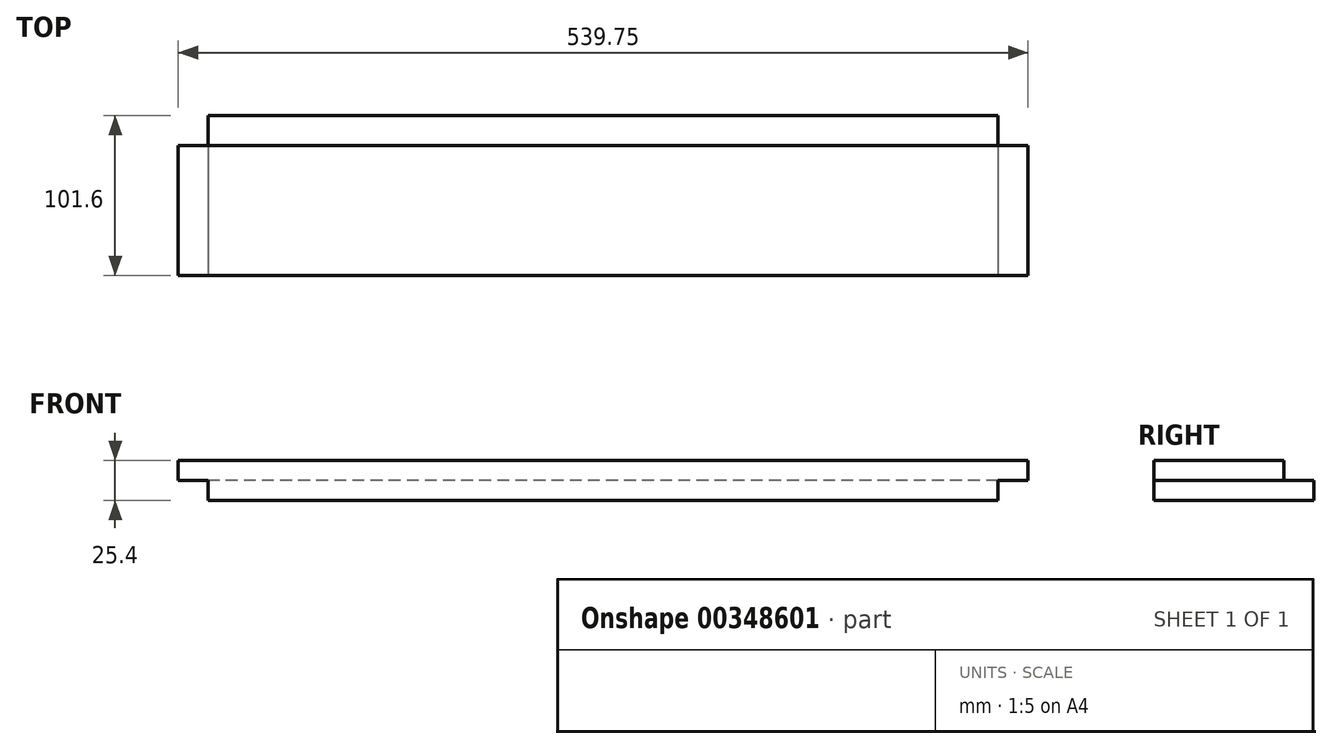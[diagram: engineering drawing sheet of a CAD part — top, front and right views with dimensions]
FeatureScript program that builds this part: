
annotation { "Feature Type Name" : "Feature", "Feature Type Description" : "" }
export const myFeature = defineFeature(function(context is Context, id is Id, definition is map)
    precondition{}
    {
        {
            var Q0;
            Q0=qCreatedBy(makeId("Top.planeOp"),FACE);
            var sketch = newSketch(context, id + "F0", { "sketchPlane" : qUnion([Q0])});
            skLineSegment(sketch, "E0.bottom", {"start": v(-320.57, -5.97) * mm, "end": v(219.18, -5.97) * mm});
            skLineSegment(sketch, "E0.top", {"start": v(-320.57, -107.57) * mm, "end": v(219.18, -107.57) * mm});
            skLineSegment(sketch, "E0.left", {"start": v(-320.57, -5.97) * mm, "end": v(-320.57, -107.57) * mm});
            skLineSegment(sketch, "E0.right", {"start": v(219.18, -5.97) * mm, "end": v(219.18, -107.57) * mm});
            skLineSegment(sketch, "E1", {"start": v(-301.52, -5.97) * mm, "end": v(-301.52, -107.57) * mm});
            skLineSegment(sketch, "E2", {"start": v(200.13, -5.97) * mm, "end": v(200.13, -107.57) * mm});
            skLineSegment(sketch, "E3", {"start": v(-320.57, -25.02) * mm, "end": v(219.18, -25.02) * mm});
            skSolve(sketch);
        }
        {
            var Q0;
            {var subQ0=sQuery(id+"F0.wireOp",EDGE,"E1");var subQ1=sQuery(id+"F0.wireOp",EDGE,"E0.top");var subQ2=makeQuery(id+"F0.imprint","INTERSECT",VERTEX,{"derivedFrom":[subQ1,subQ0]});Q0=makeQuery(id+"F0.imprint","IMPRINT",FACE,{"disambiguationData":[TD([[makeQuery(id+"F0.imprint","IMPRINT",EDGE,{"disambiguationData":[TD([[subQ2,-1.0]])],"derivedFrom":subQ1}),1.0]])]});}
            var Q1;
            {var subQ0=sQuery(id+"F0.wireOp",EDGE,"E0.left");var subQ1=sQuery(id+"F0.wireOp",EDGE,"E0.top");var subQ2=makeQuery(id+"F0.imprint","INTERSECT",VERTEX,{"derivedFrom":[subQ1,subQ0]});Q1=makeQuery(id+"F0.imprint","IMPRINT",FACE,{"disambiguationData":[TD([[makeQuery(id+"F0.imprint","IMPRINT",EDGE,{"disambiguationData":[TD([[subQ2,-1.0]])],"derivedFrom":subQ1}),1.0]])]});}
            var Q2;
            {var subQ0=sQuery(id+"F0.wireOp",EDGE,"E1");var subQ1=sQuery(id+"F0.wireOp",EDGE,"E0.bottom");var subQ2=makeQuery(id+"F0.imprint","INTERSECT",VERTEX,{"derivedFrom":[subQ1,subQ0]});Q2=makeQuery(id+"F0.imprint","IMPRINT",FACE,{"disambiguationData":[TD([[makeQuery(id+"F0.imprint","IMPRINT",EDGE,{"disambiguationData":[TD([[subQ2,-1.0]])],"derivedFrom":subQ1}),-1.0]])]});}
            var Q3;
            {var subQ0=sQuery(id+"F0.wireOp",EDGE,"E0.right");var subQ1=sQuery(id+"F0.wireOp",EDGE,"E0.top");var subQ2=makeQuery(id+"F0.imprint","INTERSECT",VERTEX,{"derivedFrom":[subQ1,subQ0]});Q3=makeQuery(id+"F0.imprint","IMPRINT",FACE,{"disambiguationData":[TD([[makeQuery(id+"F0.imprint","IMPRINT",EDGE,{"disambiguationData":[TD([[subQ2,1.0]])],"derivedFrom":subQ1}),1.0]])]});}
            extrude(context, id + "F1", {"entities" : qUnion([Q0, Q1, Q2, Q3]), "depth" : 12.7 * mm});
        }
        {
            var Q0;
            {var subQ0=sQuery(id+"F0.wireOp",EDGE,"E1");var subQ1=sQuery(id+"F0.wireOp",EDGE,"E0.top");var subQ2=makeQuery(id+"F0.imprint","INTERSECT",VERTEX,{"derivedFrom":[subQ1,subQ0]});Q0=makeQuery(id+"F0.imprint","IMPRINT",FACE,{"disambiguationData":[TD([[makeQuery(id+"F0.imprint","IMPRINT",EDGE,{"disambiguationData":[TD([[subQ2,-1.0]])],"derivedFrom":subQ1}),1.0]])]});}
            var Q1;
            {var subQ0=sQuery(id+"F0.wireOp",EDGE,"E0.left");var subQ1=sQuery(id+"F0.wireOp",EDGE,"E0.top");var subQ2=makeQuery(id+"F0.imprint","INTERSECT",VERTEX,{"derivedFrom":[subQ1,subQ0]});Q1=makeQuery(id+"F0.imprint","IMPRINT",FACE,{"disambiguationData":[TD([[makeQuery(id+"F0.imprint","IMPRINT",EDGE,{"disambiguationData":[TD([[subQ2,-1.0]])],"derivedFrom":subQ1}),1.0]])]});}
            var Q2;
            {var subQ0=sQuery(id+"F0.wireOp",EDGE,"E0.right");var subQ1=sQuery(id+"F0.wireOp",EDGE,"E0.top");var subQ2=makeQuery(id+"F0.imprint","INTERSECT",VERTEX,{"derivedFrom":[subQ1,subQ0]});Q2=makeQuery(id+"F0.imprint","IMPRINT",FACE,{"disambiguationData":[TD([[makeQuery(id+"F0.imprint","IMPRINT",EDGE,{"disambiguationData":[TD([[subQ2,1.0]])],"derivedFrom":subQ1}),1.0]])]});}
            extrude(context, id + "F2", {"entities" : qUnion([Q0, Q1, Q2]), "operationType" : NewBodyOperationType.ADD, "depth" : 25.4 * mm});
        }
        {
            var Q0;
            {var subQ0=sQuery(id+"F0.wireOp",EDGE,"E0.left");var subQ1=sQuery(id+"F0.wireOp",EDGE,"E0.top");var subQ2=makeQuery(id+"F0.imprint","INTERSECT",VERTEX,{"derivedFrom":[subQ1,subQ0]});Q0=makeQuery(id+"F0.imprint","IMPRINT",FACE,{"disambiguationData":[TD([[makeQuery(id+"F0.imprint","IMPRINT",EDGE,{"disambiguationData":[TD([[subQ2,-1.0]])],"derivedFrom":subQ1}),1.0]])]});}
            var Q1;
            {var subQ0=sQuery(id+"F0.wireOp",EDGE,"E0.right");var subQ1=sQuery(id+"F0.wireOp",EDGE,"E0.top");var subQ2=makeQuery(id+"F0.imprint","INTERSECT",VERTEX,{"derivedFrom":[subQ1,subQ0]});Q1=makeQuery(id+"F0.imprint","IMPRINT",FACE,{"disambiguationData":[TD([[makeQuery(id+"F0.imprint","IMPRINT",EDGE,{"disambiguationData":[TD([[subQ2,1.0]])],"derivedFrom":subQ1}),1.0]])]});}
            extrude(context, id + "F3", {"entities" : qUnion([Q0, Q1]), "operationType" : NewBodyOperationType.REMOVE, "oppositeDirection" : true, "depth" : -12.7 * mm});
        }
    });
